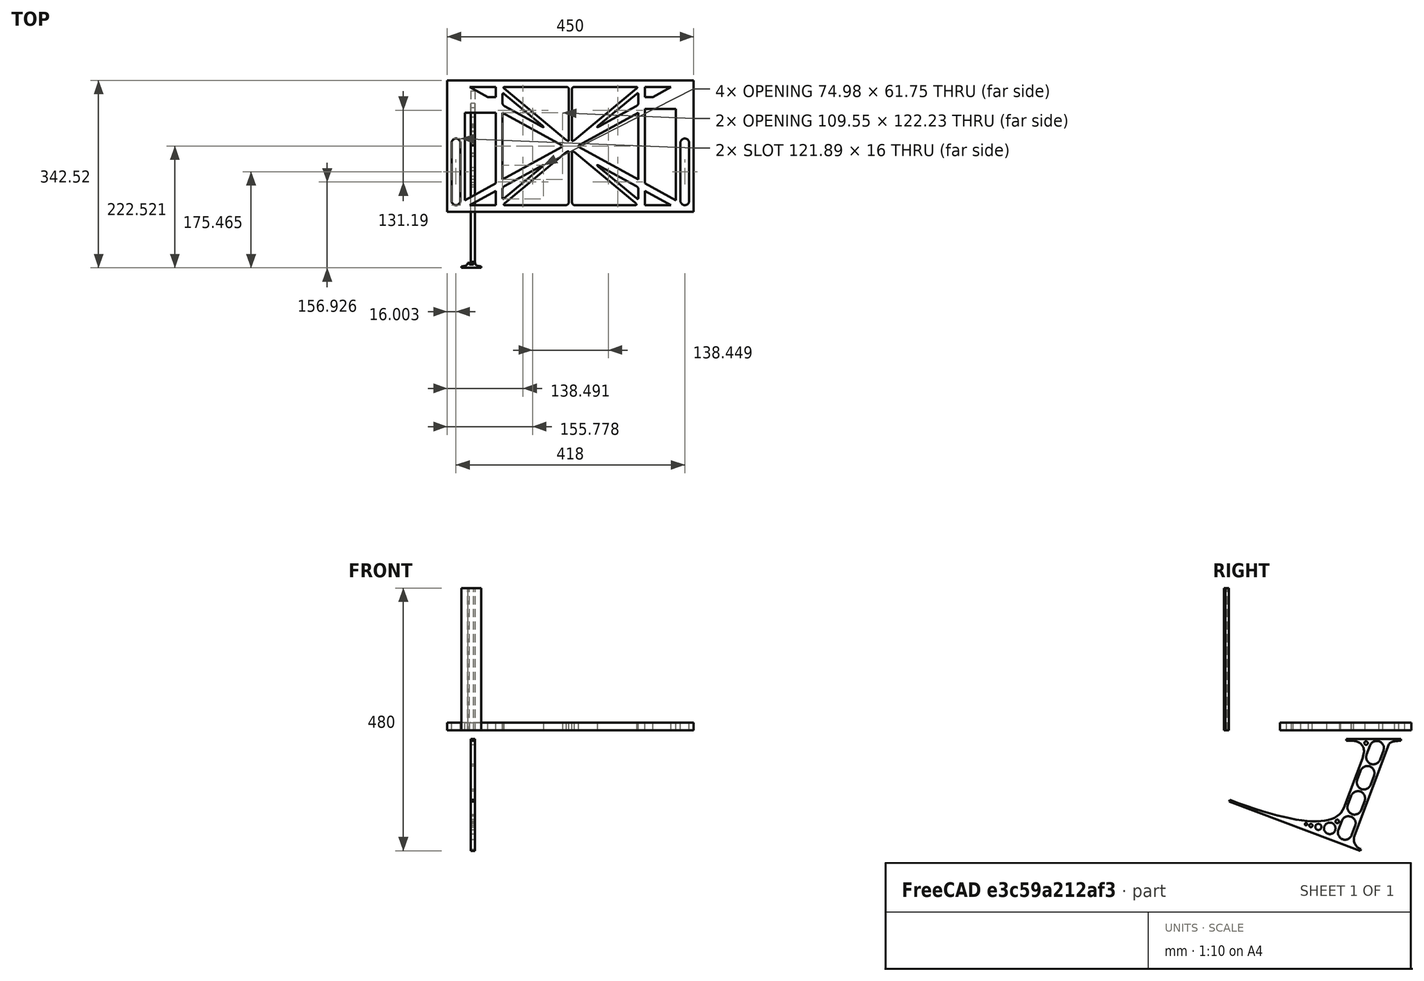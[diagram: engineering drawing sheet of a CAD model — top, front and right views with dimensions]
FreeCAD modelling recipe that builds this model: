
FCSTD DOCUMENT  (FreeCAD 0.19R0.19.2)
Label: laptopStand086
License: All rights reserved
LicenseURL: http://en.wikipedia.org/wiki/All_rights_reserved
objects: Sketcher::SketchObject×3, Part::Extrusion×3
note: 6 computed .brp shape members not serialized (recipe doc carries the construction recipe); baked Part::Feature solids carry a one-line shape summary decoded from their .brp

FEATURE [Sketcher::SketchObject] Sketch
  FullyConstrained = true
  sketch-geometry (224):
    g0: LineSegment StartX=-10.9272 StartY=-82.7794 StartZ=0 EndX=46.0728 EndY=-51.4823 EndZ=0
    g1: LineSegment StartX=366.073 StartY=-91.7794 StartZ=0 EndX=318.073 EndY=-65.424 EndZ=0
    g2: LineSegment StartX=-10.9272 StartY=77.3346 StartZ=0 EndX=-10.9272 EndY=-82.7794 EndZ=0
    g3: LineSegment StartX=375.073 StartY=-82.7794 StartZ=0 EndX=375.073 EndY=83.9235 EndZ=0
    g4: LineSegment StartX=-1.92719 StartY=-91.7794 StartZ=0 EndX=46.0728 EndY=-91.7794 EndZ=0
    g5: LineSegment StartX=318.073 StartY=124.221 StartZ=0 EndX=366.073 EndY=124.221 EndZ=0
    g6: LineSegment StartX=306.073 StartY=77.3346 StartZ=0 EndX=306.073 EndY=-44.8935 EndZ=0
    g7: LineSegment StartX=318.073 StartY=83.9235 StartZ=0 EndX=318.073 EndY=-51.4823 EndZ=0
    g8: LineSegment StartX=318.073 StartY=-51.4823 StartZ=0 EndX=375.073 EndY=-82.7794 EndZ=0
    g9: LineSegment StartX=318.073 StartY=-65.424 StartZ=0 EndX=318.073 EndY=-91.7794 EndZ=0
    g10: LineSegment StartX=318.073 StartY=-91.7794 StartZ=0 EndX=366.073 EndY=-91.7794 EndZ=0
    g11: LineSegment StartX=58.0728 StartY=-44.8935 StartZ=0 EndX=58.0728 EndY=77.3346 EndZ=0
    g12: LineSegment StartX=46.0728 StartY=-65.424 StartZ=0 EndX=-1.92719 EndY=-91.7794 EndZ=0
    g13: LineSegment StartX=46.0728 StartY=-65.424 StartZ=0 EndX=46.0728 EndY=-91.7794 EndZ=0
    g14: LineSegment StartX=46.0728 StartY=77.3346 StartZ=0 EndX=46.0728 EndY=-51.4823 EndZ=0
    g15: LineSegment StartX=-42.9272 StartY=136.221 StartZ=0 EndX=-42.9272 EndY=-103.779 EndZ=0
    g16: LineSegment StartX=407.073 StartY=136.221 StartZ=0 EndX=407.073 EndY=-103.779 EndZ=0
    g17: ArcOfCircle CenterX=-26.9272 CenterY=22.1087 CenterZ=0 NormalX=0 NormalY=0 NormalZ=1 AngleXU=0 Radius=8 StartAngle=1e-16 EndAngle=3.14159
    g18: ArcOfCircle CenterX=-26.9272 CenterY=-83.7794 CenterZ=0 NormalX=0 NormalY=0 NormalZ=1 AngleXU=0 Radius=8 StartAngle=3.14159 EndAngle=6.28319
    g19: LineSegment StartX=-34.9272 StartY=22.1087 StartZ=0 EndX=-34.9272 EndY=-83.7794 EndZ=0
    g20: LineSegment StartX=-18.9272 StartY=22.1087 StartZ=0 EndX=-18.9272 EndY=-83.7794 EndZ=0
    g21: ArcOfCircle CenterX=391.073 CenterY=22.1087 CenterZ=0 NormalX=0 NormalY=0 NormalZ=1 AngleXU=0 Radius=8 StartAngle=-4.4e-15 EndAngle=3.14159
    g22: LineSegment StartX=399.073 StartY=22.1087 StartZ=0 EndX=399.073 EndY=-83.7794 EndZ=0
    g23: LineSegment StartX=383.073 StartY=22.1087 StartZ=0 EndX=383.073 EndY=-83.7794 EndZ=0
    g24: ArcOfCircle CenterX=391.073 CenterY=-83.7794 CenterZ=0 NormalX=0 NormalY=0 NormalZ=1 AngleXU=0 Radius=8 StartAngle=3.14159 EndAngle=6.28319
    g25: Circle CenterX=175.022 CenterY=27.0628 CenterZ=0 NormalX=0 NormalY=0 NormalZ=1 AngleXU=0 Radius=1
    g26: Circle CenterX=179.022 CenterY=24.8665 CenterZ=0 NormalX=0 NormalY=0 NormalZ=1 AngleXU=0 Radius=1
    g27: Circle CenterX=179.022 CenterY=27.0628 CenterZ=0 NormalX=0 NormalY=0 NormalZ=1 AngleXU=0 Radius=1
    g28: BSplineCurve PolesCount=3 KnotsCount=2 Degree=2 IsPeriodic=0
    g29: GeomPoint X=175.022 Y=27.0628 Z=0
    g30: GeomPoint X=179.022 Y=27.0628 Z=0
    g31: Circle CenterX=189.124 CenterY=27.0628 CenterZ=0 NormalX=0 NormalY=0 NormalZ=1 AngleXU=0 Radius=1
    g32: Circle CenterX=185.124 CenterY=24.8665 CenterZ=0 NormalX=0 NormalY=0 NormalZ=1 AngleXU=0 Radius=1
    g33: Circle CenterX=185.124 CenterY=27.0628 CenterZ=0 NormalX=0 NormalY=0 NormalZ=1 AngleXU=0 Radius=1
    g34: BSplineCurve PolesCount=3 KnotsCount=2 Degree=2 IsPeriodic=0
    g35: GeomPoint X=189.124 Y=27.0628 Z=0
    g36: GeomPoint X=185.124 Y=27.0628 Z=0
    g37: Circle CenterX=175.022 CenterY=5.37834 CenterZ=0 NormalX=0 NormalY=0 NormalZ=1 AngleXU=0 Radius=1
    g38: Circle CenterX=179.022 CenterY=7.57463 CenterZ=0 NormalX=0 NormalY=0 NormalZ=1 AngleXU=0 Radius=1
    g39: Circle CenterX=179.022 CenterY=5.34704 CenterZ=0 NormalX=0 NormalY=0 NormalZ=1 AngleXU=0 Radius=1
    g40: BSplineCurve PolesCount=3 KnotsCount=2 Degree=2 IsPeriodic=0
    g41: GeomPoint X=175.022 Y=5.37834 Z=0
    g42: GeomPoint X=179.022 Y=5.34704 Z=0
    g43: Circle CenterX=189.124 CenterY=5.37834 CenterZ=0 NormalX=0 NormalY=0 NormalZ=1 AngleXU=0 Radius=1
    g44: Circle CenterX=185.124 CenterY=7.57463 CenterZ=0 NormalX=0 NormalY=0 NormalZ=1 AngleXU=0 Radius=1
    g45: Circle CenterX=185.124 CenterY=5.34704 CenterZ=0 NormalX=0 NormalY=0 NormalZ=1 AngleXU=0 Radius=1
    g46: BSplineCurve PolesCount=3 KnotsCount=2 Degree=2 IsPeriodic=0
    g47: GeomPoint X=189.124 Y=5.37834 Z=0
    g48: GeomPoint X=185.124 Y=5.34704 Z=0
    g49: Circle CenterX=165.871 CenterY=18.1458 CenterZ=0 NormalX=0 NormalY=0 NormalZ=1 AngleXU=0 Radius=1
    g50: Circle CenterX=169.377 CenterY=16.2206 CenterZ=0 NormalX=0 NormalY=0 NormalZ=1 AngleXU=0 Radius=1
    g51: Circle CenterX=165.871 CenterY=14.2954 CenterZ=0 NormalX=0 NormalY=0 NormalZ=1 AngleXU=0 Radius=1
    g52: BSplineCurve PolesCount=3 KnotsCount=2 Degree=2 IsPeriodic=0
    g53: GeomPoint X=165.871 Y=18.1458 Z=0
    g54: GeomPoint X=165.871 Y=14.2954 Z=0
    g55: Circle CenterX=198.275 CenterY=18.1458 CenterZ=0 NormalX=0 NormalY=0 NormalZ=1 AngleXU=0 Radius=1
    g56: Circle CenterX=194.768 CenterY=16.2206 CenterZ=0 NormalX=0 NormalY=0 NormalZ=1 AngleXU=0 Radius=1
    g57: Circle CenterX=198.275 CenterY=14.2954 CenterZ=0 NormalX=0 NormalY=0 NormalZ=1 AngleXU=0 Radius=1
    g58: BSplineCurve PolesCount=3 KnotsCount=2 Degree=2 IsPeriodic=0
    g59: GeomPoint X=198.275 Y=18.1458 Z=0
    g60: GeomPoint X=198.275 Y=14.2954 Z=0
    g61: LineSegment StartX=165.871 StartY=18.1458 StartZ=0 EndX=58.0728 EndY=77.3346 EndZ=0
    g62: LineSegment StartX=58.0728 StartY=-44.8935 StartZ=0 EndX=165.871 EndY=14.2954 EndZ=0
    g63: LineSegment StartX=198.275 StartY=18.1458 StartZ=0 EndX=306.073 EndY=77.3346 EndZ=0
    g64: LineSegment StartX=198.275 StartY=14.2954 StartZ=0 EndX=306.073 EndY=-44.8935 EndZ=0
    g65: LineSegment StartX=407.073 StartY=-103.779 StartZ=0 EndX=-42.9272 EndY=-103.779 EndZ=0
    g66: LineSegment StartX=407.073 StartY=136.221 StartZ=0 EndX=-42.9272 EndY=136.221 EndZ=0
    g67: LineSegment StartX=46.0728 StartY=77.3346 StartZ=0 EndX=-10.9272 EndY=77.3346 EndZ=0
    g68: LineSegment StartX=46.0728 StartY=105.865 StartZ=0 EndX=31.5028 EndY=105.865 EndZ=0
    g69: LineSegment StartX=46.0728 StartY=124.221 StartZ=0 EndX=46.0728 EndY=105.865 EndZ=0
    g70: LineSegment StartX=-1.92719 StartY=124.221 StartZ=0 EndX=31.5028 EndY=105.865 EndZ=0
    g71: LineSegment StartX=46.0728 StartY=124.221 StartZ=0 EndX=-1.92719 EndY=124.221 EndZ=0
    g72: LineSegment StartX=318.073 StartY=83.9235 StartZ=0 EndX=375.073 EndY=83.9235 EndZ=0
    g73: LineSegment StartX=318.073 StartY=105.865 StartZ=0 EndX=332.643 EndY=105.865 EndZ=0
    g74: LineSegment StartX=332.643 StartY=105.865 StartZ=0 EndX=366.073 EndY=124.221 EndZ=0
    g75: LineSegment StartX=318.073 StartY=124.221 StartZ=0 EndX=318.073 EndY=105.865 EndZ=0
    g76: Circle CenterX=125.607 CenterY=54.1951 CenterZ=0 NormalX=0 NormalY=0 NormalZ=1 AngleXU=0 Radius=1
    g77: Circle CenterX=139.632 CenterY=46.4944 CenterZ=0 NormalX=0 NormalY=0 NormalZ=1 AngleXU=0 Radius=1
    g78: Circle CenterX=127.326 CenterY=56.7187 CenterZ=0 NormalX=0 NormalY=0 NormalZ=1 AngleXU=0 Radius=1
    g79: BSplineCurve PolesCount=3 KnotsCount=2 Degree=2 IsPeriodic=0
    g80: GeomPoint X=125.607 Y=54.1951 Z=0
    g81: GeomPoint X=127.326 Y=56.7187 Z=0
    g82: Circle CenterX=236.821 CenterY=56.7187 CenterZ=0 NormalX=0 NormalY=0 NormalZ=1 AngleXU=0 Radius=1
    g83: Circle CenterX=224.513 CenterY=46.4944 CenterZ=0 NormalX=0 NormalY=0 NormalZ=1 AngleXU=0 Radius=1
    g84: Circle CenterX=238.538 CenterY=54.1951 CenterZ=0 NormalX=0 NormalY=0 NormalZ=1 AngleXU=0 Radius=1
    g85: BSplineCurve PolesCount=3 KnotsCount=2 Degree=2 IsPeriodic=0
    g86: GeomPoint X=236.821 Y=56.7187 Z=0
    g87: GeomPoint X=238.538 Y=54.1951 Z=0
    g88: Circle CenterX=238.538 CenterY=-21.7539 CenterZ=0 NormalX=0 NormalY=0 NormalZ=1 AngleXU=0 Radius=1
    g89: Circle CenterX=224.513 CenterY=-14.0532 CenterZ=0 NormalX=0 NormalY=0 NormalZ=1 AngleXU=0 Radius=1
    g90: Circle CenterX=236.821 CenterY=-24.2775 CenterZ=0 NormalX=0 NormalY=0 NormalZ=1 AngleXU=0 Radius=1
    g91: BSplineCurve PolesCount=3 KnotsCount=2 Degree=2 IsPeriodic=0
    g92: GeomPoint X=238.538 Y=-21.7539 Z=0
    g93: GeomPoint X=236.821 Y=-24.2775 Z=0
    g94: Circle CenterX=125.607 CenterY=-21.7539 CenterZ=0 NormalX=0 NormalY=0 NormalZ=1 AngleXU=0 Radius=1
    g95: Circle CenterX=139.632 CenterY=-14.0532 CenterZ=0 NormalX=0 NormalY=0 NormalZ=1 AngleXU=0 Radius=1
    g96: Circle CenterX=127.325 CenterY=-24.2775 CenterZ=0 NormalX=0 NormalY=0 NormalZ=1 AngleXU=0 Radius=1
    g97: BSplineCurve PolesCount=3 KnotsCount=2 Degree=2 IsPeriodic=0
    g98: GeomPoint X=125.607 Y=-21.7539 Z=0
    g99: GeomPoint X=127.325 Y=-24.2775 Z=0
    g100: Circle CenterX=302.996 CenterY=111.695 CenterZ=0 NormalX=0 NormalY=0 NormalZ=1 AngleXU=0 Radius=1
    g101: Circle CenterX=306.073 CenterY=114.251 CenterZ=0 NormalX=0 NormalY=0 NormalZ=1 AngleXU=0 Radius=1
    g102: Circle CenterX=306.073 CenterY=110.251 CenterZ=0 NormalX=0 NormalY=0 NormalZ=1 AngleXU=0 Radius=1
    g103: BSplineCurve PolesCount=3 KnotsCount=2 Degree=2 IsPeriodic=0
    g104: GeomPoint X=302.996 Y=111.695 Z=0
    g105: GeomPoint X=306.073 Y=110.251 Z=0
    g106: Circle CenterX=306.073 CenterY=95.2763 CenterZ=0 NormalX=0 NormalY=0 NormalZ=1 AngleXU=0 Radius=1
    g107: Circle CenterX=306.073 CenterY=91.2763 CenterZ=0 NormalX=0 NormalY=0 NormalZ=1 AngleXU=0 Radius=1
    g108: Circle CenterX=302.567 CenterY=89.3511 CenterZ=0 NormalX=0 NormalY=0 NormalZ=1 AngleXU=0 Radius=1
    g109: BSplineCurve PolesCount=3 KnotsCount=2 Degree=2 IsPeriodic=0
    g110: GeomPoint X=306.073 Y=95.2763 Z=0
    g111: GeomPoint X=302.567 Y=89.3511 Z=0
    g112: LineSegment StartX=306.073 StartY=110.251 StartZ=0 EndX=306.073 EndY=95.2763 EndZ=0
    g113: LineSegment StartX=302.996 StartY=111.695 StartZ=0 EndX=236.821 EndY=56.7187 EndZ=0
    g114: LineSegment StartX=238.538 StartY=54.1951 StartZ=0 EndX=302.567 EndY=89.3511 EndZ=0
    g115: Circle CenterX=61.1496 CenterY=111.695 CenterZ=0 NormalX=0 NormalY=0 NormalZ=1 AngleXU=0 Radius=1
    g116: Circle CenterX=58.0728 CenterY=114.251 CenterZ=0 NormalX=0 NormalY=0 NormalZ=1 AngleXU=0 Radius=1
    g117: Circle CenterX=58.0728 CenterY=110.251 CenterZ=0 NormalX=0 NormalY=0 NormalZ=1 AngleXU=0 Radius=1
    g118: BSplineCurve PolesCount=3 KnotsCount=2 Degree=2 IsPeriodic=0
    g119: GeomPoint X=61.1496 Y=111.695 Z=0
    g120: GeomPoint X=58.0728 Y=110.251 Z=0
    g121: Circle CenterX=61.5791 CenterY=89.3511 CenterZ=0 NormalX=0 NormalY=0 NormalZ=1 AngleXU=0 Radius=1
    g122: Circle CenterX=58.0728 CenterY=91.2763 CenterZ=0 NormalX=0 NormalY=0 NormalZ=1 AngleXU=0 Radius=1
    g123: Circle CenterX=58.0728 CenterY=95.2763 CenterZ=0 NormalX=0 NormalY=0 NormalZ=1 AngleXU=0 Radius=1
    g124: BSplineCurve PolesCount=3 KnotsCount=2 Degree=2 IsPeriodic=0
    g125: GeomPoint X=61.5791 Y=89.3511 Z=0
    g126: GeomPoint X=58.0728 Y=95.2763 Z=0
    g127: LineSegment StartX=58.0728 StartY=110.251 StartZ=0 EndX=58.0728 EndY=95.2763 EndZ=0
    g128: LineSegment StartX=61.1496 StartY=111.695 StartZ=0 EndX=127.326 EndY=56.7187 EndZ=0
    g129: LineSegment StartX=125.607 StartY=54.1951 StartZ=0 EndX=61.5791 EndY=89.3511 EndZ=0
    g130: Circle CenterX=61.5791 CenterY=-56.9099 CenterZ=0 NormalX=0 NormalY=0 NormalZ=1 AngleXU=0 Radius=1
    g131: Circle CenterX=58.0728 CenterY=-58.8351 CenterZ=0 NormalX=0 NormalY=0 NormalZ=1 AngleXU=0 Radius=1
    g132: Circle CenterX=58.0728 CenterY=-62.8351 CenterZ=0 NormalX=0 NormalY=0 NormalZ=1 AngleXU=0 Radius=1
    g133: BSplineCurve PolesCount=3 KnotsCount=2 Degree=2 IsPeriodic=0
    g134: GeomPoint X=61.5791 Y=-56.9099 Z=0
    g135: GeomPoint X=58.0728 Y=-62.8351 Z=0
    g136: Circle CenterX=58.0728 CenterY=-77.8102 CenterZ=0 NormalX=0 NormalY=0 NormalZ=1 AngleXU=0 Radius=1
    g137: Circle CenterX=58.0728 CenterY=-81.8102 CenterZ=0 NormalX=0 NormalY=0 NormalZ=1 AngleXU=0 Radius=1
    g138: Circle CenterX=61.1496 CenterY=-79.2541 CenterZ=0 NormalX=0 NormalY=0 NormalZ=1 AngleXU=0 Radius=1
    g139: BSplineCurve PolesCount=3 KnotsCount=2 Degree=2 IsPeriodic=0
    g140: GeomPoint X=58.0728 Y=-77.8102 Z=0
    g141: GeomPoint X=61.1496 Y=-79.2541 Z=0
    g142: LineSegment StartX=58.0728 StartY=-62.8351 StartZ=0 EndX=58.0728 EndY=-77.8102 EndZ=0
    g143: LineSegment StartX=61.1496 StartY=-79.2541 StartZ=0 EndX=127.325 EndY=-24.2775 EndZ=0
    g144: LineSegment StartX=125.607 StartY=-21.7539 StartZ=0 EndX=61.5791 EndY=-56.9099 EndZ=0
    g145: Circle CenterX=302.567 CenterY=-56.9099 CenterZ=0 NormalX=0 NormalY=0 NormalZ=1 AngleXU=0 Radius=1
    g146: Circle CenterX=306.073 CenterY=-58.8351 CenterZ=0 NormalX=0 NormalY=0 NormalZ=1 AngleXU=0 Radius=1
    g147: Circle CenterX=306.073 CenterY=-62.8351 CenterZ=0 NormalX=0 NormalY=0 NormalZ=1 AngleXU=0 Radius=1
    g148: BSplineCurve PolesCount=3 KnotsCount=2 Degree=2 IsPeriodic=0
    g149: GeomPoint X=302.567 Y=-56.9099 Z=0
    g150: GeomPoint X=306.073 Y=-62.8351 Z=0
    g151: Circle CenterX=302.996 CenterY=-79.2541 CenterZ=0 NormalX=0 NormalY=0 NormalZ=1 AngleXU=0 Radius=1
    g152: Circle CenterX=306.073 CenterY=-81.8102 CenterZ=0 NormalX=0 NormalY=0 NormalZ=1 AngleXU=0 Radius=1
    g153: Circle CenterX=306.073 CenterY=-77.8102 CenterZ=0 NormalX=0 NormalY=0 NormalZ=1 AngleXU=0 Radius=1
    g154: BSplineCurve PolesCount=3 KnotsCount=2 Degree=2 IsPeriodic=0
    g155: GeomPoint X=302.996 Y=-79.2541 Z=0
    g156: GeomPoint X=306.073 Y=-77.8102 Z=0
    g157: LineSegment StartX=306.073 StartY=-62.8351 StartZ=0 EndX=306.073 EndY=-77.8102 EndZ=0
    g158: LineSegment StartX=302.996 StartY=-79.2541 StartZ=0 EndX=236.821 EndY=-24.2775 EndZ=0
    g159: LineSegment StartX=238.538 StartY=-21.7539 StartZ=0 EndX=302.567 EndY=-56.9099 EndZ=0
    g160: Circle CenterX=61.6457 CenterY=-88.8112 CenterZ=0 NormalX=0 NormalY=0 NormalZ=1 AngleXU=0 Radius=1
    g161: Circle CenterX=58.0728 CenterY=-91.7794 CenterZ=0 NormalX=0 NormalY=0 NormalZ=1 AngleXU=0 Radius=1
    g162: Circle CenterX=63.9135 CenterY=-91.7794 CenterZ=0 NormalX=0 NormalY=0 NormalZ=1 AngleXU=0 Radius=1
    g163: BSplineCurve PolesCount=3 KnotsCount=2 Degree=2 IsPeriodic=0
    g164: GeomPoint X=61.6457 Y=-88.8112 Z=0
    g165: GeomPoint X=63.9135 Y=-91.7794 Z=0
    g166: Circle CenterX=179.022 CenterY=-85.8163 CenterZ=0 NormalX=0 NormalY=0 NormalZ=1 AngleXU=0 Radius=1
    g167: Circle CenterX=179.022 CenterY=-91.7794 CenterZ=0 NormalX=0 NormalY=0 NormalZ=1 AngleXU=0 Radius=1
    g168: Circle CenterX=171.895 CenterY=-91.7794 CenterZ=0 NormalX=0 NormalY=0 NormalZ=1 AngleXU=0 Radius=1
    g169: BSplineCurve PolesCount=3 KnotsCount=2 Degree=2 IsPeriodic=0
    g170: GeomPoint X=179.022 Y=-85.8163 Z=0
    g171: GeomPoint X=171.895 Y=-91.7794 Z=0
    g172: Circle CenterX=185.124 CenterY=-86.2028 CenterZ=0 NormalX=0 NormalY=0 NormalZ=1 AngleXU=0 Radius=1
    g173: Circle CenterX=185.124 CenterY=-91.7794 CenterZ=0 NormalX=0 NormalY=0 NormalZ=1 AngleXU=0 Radius=1
    g174: Circle CenterX=191.747 CenterY=-91.7794 CenterZ=0 NormalX=0 NormalY=0 NormalZ=1 AngleXU=0 Radius=1
    g175: BSplineCurve PolesCount=3 KnotsCount=2 Degree=2 IsPeriodic=0
    g176: GeomPoint X=185.124 Y=-86.2028 Z=0
    g177: GeomPoint X=191.747 Y=-91.7794 Z=0
    g178: Circle CenterX=299.888 CenterY=-86.6413 CenterZ=0 NormalX=0 NormalY=0 NormalZ=1 AngleXU=0 Radius=1
    g179: Circle CenterX=306.073 CenterY=-91.7794 CenterZ=0 NormalX=0 NormalY=0 NormalZ=1 AngleXU=0 Radius=1
    g180: Circle CenterX=298.776 CenterY=-91.7794 CenterZ=0 NormalX=0 NormalY=0 NormalZ=1 AngleXU=0 Radius=1
    g181: BSplineCurve PolesCount=3 KnotsCount=2 Degree=2 IsPeriodic=0
    g182: GeomPoint X=299.888 Y=-86.6413 Z=0
    g183: GeomPoint X=298.776 Y=-91.7794 Z=0
    g184: LineSegment StartX=189.124 StartY=5.37834 StartZ=0 EndX=299.888 EndY=-86.6413 EndZ=0
    g185: LineSegment StartX=298.776 StartY=-91.7794 StartZ=0 EndX=191.747 EndY=-91.7794 EndZ=0
    g186: LineSegment StartX=185.124 StartY=-86.2028 StartZ=0 EndX=185.124 EndY=5.34704 EndZ=0
    g187: LineSegment StartX=179.022 StartY=5.34704 StartZ=0 EndX=179.022 EndY=-85.8163 EndZ=0
    g188: LineSegment StartX=171.895 StartY=-91.7794 StartZ=0 EndX=63.9135 EndY=-91.7794 EndZ=0
    g189: LineSegment StartX=61.6457 StartY=-88.8112 StartZ=0 EndX=175.022 EndY=5.37834 EndZ=0
    g190: Circle CenterX=302.073 CenterY=124.221 CenterZ=0 NormalX=0 NormalY=0 NormalZ=1 AngleXU=0 Radius=1
    g191: Circle CenterX=306.073 CenterY=124.221 CenterZ=0 NormalX=0 NormalY=0 NormalZ=1 AngleXU=0 Radius=1
    g192: Circle CenterX=302.996 CenterY=121.665 CenterZ=0 NormalX=0 NormalY=0 NormalZ=1 AngleXU=0 Radius=1
    g193: BSplineCurve PolesCount=3 KnotsCount=2 Degree=2 IsPeriodic=0
    g194: GeomPoint X=302.073 Y=124.221 Z=0
    g195: GeomPoint X=302.996 Y=121.665 Z=0
    g196: Circle CenterX=189.124 CenterY=124.221 CenterZ=0 NormalX=0 NormalY=0 NormalZ=1 AngleXU=0 Radius=1
    g197: Circle CenterX=185.124 CenterY=124.221 CenterZ=0 NormalX=0 NormalY=0 NormalZ=1 AngleXU=0 Radius=1
    g198: Circle CenterX=185.124 CenterY=120.221 CenterZ=0 NormalX=0 NormalY=0 NormalZ=1 AngleXU=0 Radius=1
    g199: BSplineCurve PolesCount=3 KnotsCount=2 Degree=2 IsPeriodic=0
    g200: GeomPoint X=189.124 Y=124.221 Z=0
    g201: GeomPoint X=185.124 Y=120.221 Z=0
    g202: Circle CenterX=175.022 CenterY=124.221 CenterZ=0 NormalX=0 NormalY=0 NormalZ=1 AngleXU=0 Radius=1
    g203: Circle CenterX=179.022 CenterY=124.221 CenterZ=0 NormalX=0 NormalY=0 NormalZ=1 AngleXU=0 Radius=1
    g204: Circle CenterX=179.022 CenterY=120.221 CenterZ=0 NormalX=0 NormalY=0 NormalZ=1 AngleXU=0 Radius=1
    g205: BSplineCurve PolesCount=3 KnotsCount=2 Degree=2 IsPeriodic=0
    g206: GeomPoint X=175.022 Y=124.221 Z=0
    g207: GeomPoint X=179.022 Y=120.221 Z=0
    g208: Circle CenterX=62.0728 CenterY=124.221 CenterZ=0 NormalX=0 NormalY=0 NormalZ=1 AngleXU=0 Radius=1
    g209: Circle CenterX=58.0728 CenterY=124.221 CenterZ=0 NormalX=0 NormalY=0 NormalZ=1 AngleXU=0 Radius=1
    g210: Circle CenterX=61.1496 CenterY=121.665 CenterZ=0 NormalX=0 NormalY=0 NormalZ=1 AngleXU=0 Radius=1
    g211: BSplineCurve PolesCount=3 KnotsCount=2 Degree=2 IsPeriodic=0
    g212: GeomPoint X=62.0728 Y=124.221 Z=0
    g213: GeomPoint X=61.1496 Y=121.665 Z=0
    g214: LineSegment StartX=62.0728 StartY=124.221 StartZ=0 EndX=175.022 EndY=124.221 EndZ=0
    g215: LineSegment StartX=179.022 StartY=120.221 StartZ=0 EndX=179.022 EndY=27.0628 EndZ=0
    g216: LineSegment StartX=185.124 StartY=27.0628 StartZ=0 EndX=185.124 EndY=120.221 EndZ=0
    g217: LineSegment StartX=189.124 StartY=124.221 StartZ=0 EndX=302.073 EndY=124.221 EndZ=0
    g218: LineSegment StartX=302.996 StartY=121.665 StartZ=0 EndX=189.124 EndY=27.0628 EndZ=0
    g219: LineSegment StartX=175.022 StartY=27.0628 StartZ=0 EndX=61.1496 EndY=121.665 EndZ=0
    g220: LineSegment StartX=58.0728 StartY=77.3346 StartZ=0 EndX=61.5791 EndY=75.4095 EndZ=0
    g221: LineSegment StartX=58.0728 StartY=77.3346 StartZ=0 EndX=58.0728 EndY=73.3346 EndZ=0
    g222: LineSegment StartX=58.0728 StartY=-44.8935 StartZ=0 EndX=58.0728 EndY=-40.8935 EndZ=0
    g223: LineSegment StartX=58.0728 StartY=-44.8935 StartZ=0 EndX=61.5791 EndY=-42.9683 EndZ=0
  constraints (387):
    c: Horizontal(g4)
    c: Horizontal(g5)
    c: Coincident(g7,g8)
    c: Coincident(g9,g1)
    c: Tangent(g7,g9)
    c: Coincident(g13,g12)
    c: Coincident(g0,g14)
    c: Block(g8)
    c: Block(g3)
    c: Block(g1)
    c: Block(g9)
    c: Block(g13)
    c: Block(g12)
    c: Block(g0)
    c: Block(g2)
    c: Block(g6)
    c: Block(g5)
    c: Block(g10)
    c: Block(g4)
    c: Vertical(g15)
    c: Vertical(g16)
    c: Block(g16)
    c: Block(g15)
    c: Tangent(g17,g20) = 1.5708
    c: Tangent(g17,g19) = -1.5708
    c: Tangent(g19,g18) = -1.5708
    c: Tangent(g20,g18) = 1.5708
    c: Vertical(g19)
    c: Equal(g17,g18)
    c: Block(g20)
    c: Block(g19)
    c: Tangent(g21,g22) = 1.5708
    c: Tangent(g22,g24) = 1.5708
    c: Equal(g21,g24)
    c: Coincident(g23,g21)
    c: Coincident(g23,g24)
    c: Block(g22)
    c: Block(g23)
    c: Weight(g25) = 1
    c: Equal(g25,g26)
    c: Equal(g25,g27)
    c: InternalAlignment(g25,g28)
    c: InternalAlignment(g26,g28)
    c: InternalAlignment(g27,g28)
    c: InternalAlignment(g29,g28)
    c: InternalAlignment(g30,g28)
    c: Weight(g31) = 1
    c: Equal(g31,g32)
    c: Equal(g31,g33)
    c: InternalAlignment(g31,g34)
    c: InternalAlignment(g32,g34)
    c: InternalAlignment(g33,g34)
    c: InternalAlignment(g35,g34)
    c: InternalAlignment(g36,g34)
    c: Block(g34)
    c: Block(g28)
    c: Weight(g37) = 1
    c: Equal(g37,g38)
    c: Equal(g37,g39)
    c: InternalAlignment(g37,g40)
    c: InternalAlignment(g38,g40)
    c: InternalAlignment(g39,g40)
    c: InternalAlignment(g41,g40)
    c: InternalAlignment(g42,g40)
    c: Weight(g43) = 1
    c: Equal(g43,g44)
    c: Equal(g43,g45)
    c: InternalAlignment(g43,g46)
    c: InternalAlignment(g44,g46)
    c: InternalAlignment(g45,g46)
    c: InternalAlignment(g47,g46)
    c: InternalAlignment(g48,g46)
    c: Block(g46)
    c: Block(g40)
    c: Weight(g49) = 1
    c: Equal(g49,g50)
    c: Equal(g49,g51)
    c: InternalAlignment(g49,g52)
    c: InternalAlignment(g50,g52)
    c: InternalAlignment(g51,g52)
    c: InternalAlignment(g53,g52)
    c: InternalAlignment(g54,g52)
    c: Weight(g55) = 1
    c: Equal(g55,g56)
    c: Equal(g55,g57)
    c: InternalAlignment(g55,g58)
    c: InternalAlignment(g56,g58)
    c: InternalAlignment(g57,g58)
    c: InternalAlignment(g59,g58)
    c: InternalAlignment(g60,g58)
    c: Block(g52)
    c: Block(g58)
    c: Coincident(g61,g52)
    c: Coincident(g61,g11)
    c: Coincident(g62,g11)
    c: Coincident(g62,g52)
    c: Coincident(g63,g58)
    c: Coincident(g63,g6)
    c: Coincident(g64,g58)
    c: Coincident(g64,g6)
    c: Block(g11)
    c: Coincident(g65,g16)
    c: Coincident(g65,g15)
    c: Horizontal(g65)
    c: Distance(g65) = 450
    c: Coincident(g66,g16)
    c: Coincident(g66,g15)
    c: Horizontal(g66)
    c: Horizontal(g67)
    c: Coincident(g14,g67)
    c: Horizontal(g68)
    c: Vertical(g69)
    c: Block(g69)
    c: Block(g68)
    c: Block(g67)
    c: Distance(g69) = 18.3554
    c: Coincident(g71,g69)
    c: Coincident(g71,g70)
    c: Horizontal(g71)
    c: Block(g71)
    c: Block(g70)
    c: Coincident(g68,g70)
    c: Coincident(g2,g67)
    c: Coincident(g72,g7)
    c: Horizontal(g72)
    c: Horizontal(g73)
    c: Block(g72)
    c: Coincident(g74,g5)
    c: Coincident(g75,g5)
    c: Coincident(g75,g73)
    c: Vertical(g75)
    c: Block(g75)
    c: Coincident(g73,g74)
    c: Block(g74)
    c: Coincident(g3,g72)
    c: Weight(g76) = 1
    c: Equal(g76,g77)
    c: Equal(g76,g78)
    c: InternalAlignment(g76,g79)
    c: InternalAlignment(g77,g79)
    c: InternalAlignment(g78,g79)
    c: InternalAlignment(g80,g79)
    c: InternalAlignment(g81,g79)
    c: Block(g79)
    c: Weight(g82) = 1
    c: Equal(g82,g83)
    c: Equal(g82,g84)
    c: InternalAlignment(g82,g85)
    c: InternalAlignment(g83,g85)
    c: InternalAlignment(g84,g85)
    c: InternalAlignment(g86,g85)
    c: InternalAlignment(g87,g85)
    c: Block(g85)
    c: Weight(g88) = 1
    c: Equal(g88,g89)
    c: Equal(g88,g90)
    c: InternalAlignment(g88,g91)
    c: InternalAlignment(g89,g91)
    c: InternalAlignment(g90,g91)
    c: InternalAlignment(g92,g91)
    c: InternalAlignment(g93,g91)
    c: Block(g91)
    c: Weight(g94) = 1
    c: Equal(g94,g95)
    c: Equal(g94,g96)
    c: InternalAlignment(g94,g97)
    c: InternalAlignment(g95,g97)
    c: InternalAlignment(g96,g97)
    c: InternalAlignment(g98,g97)
    c: InternalAlignment(g99,g97)
    c: Block(g97)
    c: Weight(g100) = 1
    c: Equal(g100,g101)
    c: Equal(g100,g102)
    c: InternalAlignment(g100,g103)
    c: InternalAlignment(g101,g103)
    c: InternalAlignment(g102,g103)
    c: InternalAlignment(g104,g103)
    c: InternalAlignment(g105,g103)
    c: Weight(g106) = 1
    c: Equal(g106,g107)
    c: Equal(g106,g108)
    c: InternalAlignment(g106,g109)
    c: InternalAlignment(g107,g109)
    c: InternalAlignment(g108,g109)
    c: InternalAlignment(g110,g109)
    c: InternalAlignment(g111,g109)
    c: Block(g103)
    c: Block(g109)
    c: Coincident(g112,g103)
    c: Coincident(g112,g109)
    c: Vertical(g112)
    c: Coincident(g113,g103)
    c: Coincident(g113,g85)
    c: Coincident(g114,g85)
    c: Coincident(g114,g109)
    c: Weight(g115) = 1
    c: Equal(g115,g116)
    c: Equal(g115,g117)
    c: InternalAlignment(g115,g118)
    c: InternalAlignment(g116,g118)
    c: InternalAlignment(g117,g118)
    c: InternalAlignment(g119,g118)
    c: InternalAlignment(g120,g118)
    c: Weight(g121) = 1
    c: Equal(g121,g122)
    c: Equal(g121,g123)
    c: InternalAlignment(g121,g124)
    c: InternalAlignment(g122,g124)
    c: InternalAlignment(g123,g124)
    c: InternalAlignment(g125,g124)
    c: InternalAlignment(g126,g124)
    c: Block(g118)
    c: Block(g124)
    c: Coincident(g127,g118)
    c: Coincident(g127,g124)
    c: Vertical(g127)
    c: Coincident(g128,g118)
    c: Coincident(g128,g79)
    c: Coincident(g129,g79)
    c: Coincident(g129,g124)
    c: Weight(g130) = 1
    c: Equal(g130,g131)
    c: Equal(g130,g132)
    c: InternalAlignment(g130,g133)
    c: InternalAlignment(g131,g133)
    c: InternalAlignment(g132,g133)
    c: InternalAlignment(g134,g133)
    c: InternalAlignment(g135,g133)
    c: Weight(g136) = 1
    c: Equal(g136,g137)
    c: Equal(g136,g138)
    c: InternalAlignment(g136,g139)
    c: InternalAlignment(g137,g139)
    c: InternalAlignment(g138,g139)
    c: InternalAlignment(g140,g139)
    c: InternalAlignment(g141,g139)
    c: Block(g133)
    c: Block(g139)
    c: Coincident(g142,g133)
    c: Coincident(g142,g139)
    c: Vertical(g142)
    c: Coincident(g143,g139)
    c: Coincident(g143,g97)
    c: Coincident(g144,g97)
    c: Coincident(g144,g133)
    c: Weight(g145) = 1
    c: Equal(g145,g146)
    c: Equal(g145,g147)
    c: InternalAlignment(g145,g148)
    c: InternalAlignment(g146,g148)
    c: InternalAlignment(g147,g148)
    c: InternalAlignment(g149,g148)
    c: InternalAlignment(g150,g148)
    c: Weight(g151) = 1
    c: Equal(g151,g152)
    c: Equal(g151,g153)
    c: InternalAlignment(g151,g154)
    c: InternalAlignment(g152,g154)
    c: InternalAlignment(g153,g154)
    c: InternalAlignment(g155,g154)
    c: InternalAlignment(g156,g154)
    c: Block(g148)
    c: Block(g154)
    c: Coincident(g157,g148)
    c: Coincident(g157,g154)
    c: Vertical(g157)
    c: Coincident(g158,g154)
    c: Coincident(g158,g91)
    c: Coincident(g159,g91)
    c: Coincident(g159,g148)
    c: Weight(g160) = 1
    c: Equal(g160,g161)
    c: Equal(g160,g162)
    c: InternalAlignment(g160,g163)
    c: InternalAlignment(g161,g163)
    c: InternalAlignment(g162,g163)
    c: InternalAlignment(g164,g163)
    c: InternalAlignment(g165,g163)
    c: Weight(g166) = 1
    c: Equal(g166,g167)
    c: Equal(g166,g168)
    c: InternalAlignment(g166,g169)
    c: InternalAlignment(g167,g169)
    c: InternalAlignment(g168,g169)
    c: InternalAlignment(g170,g169)
    c: InternalAlignment(g171,g169)
    c: Weight(g172) = 1
    c: Equal(g172,g173)
    c: Equal(g172,g174)
    c: InternalAlignment(g172,g175)
    c: InternalAlignment(g173,g175)
    c: InternalAlignment(g174,g175)
    c: InternalAlignment(g176,g175)
    c: InternalAlignment(g177,g175)
    c: Weight(g178) = 1
    c: Equal(g178,g179)
    c: Equal(g178,g180)
    c: InternalAlignment(g178,g181)
    c: InternalAlignment(g179,g181)
    c: InternalAlignment(g180,g181)
    c: InternalAlignment(g182,g181)
    c: InternalAlignment(g183,g181)
    c: Block(g181)
    c: Block(g175)
    c: Block(g169)
    c: Block(g163)
    c: Coincident(g184,g46)
    c: Coincident(g184,g181)
    c: Coincident(g185,g181)
    c: Coincident(g185,g175)
    c: Horizontal(g185)
    c: Coincident(g186,g175)
    c: Coincident(g186,g46)
    c: Vertical(g186)
    c: Coincident(g187,g40)
    c: Coincident(g187,g169)
    c: Vertical(g187)
    c: Coincident(g188,g169)
    c: Coincident(g188,g163)
    c: Horizontal(g188)
    c: Coincident(g189,g163)
    c: Coincident(g189,g40)
    c: Weight(g190) = 1
    c: Equal(g190,g191)
    c: Equal(g190,g192)
    c: InternalAlignment(g190,g193)
    c: InternalAlignment(g191,g193)
    c: InternalAlignment(g192,g193)
    c: InternalAlignment(g194,g193)
    c: InternalAlignment(g195,g193)
    c: Weight(g196) = 1
    c: Equal(g196,g197)
    c: Equal(g196,g198)
    c: InternalAlignment(g196,g199)
    c: InternalAlignment(g197,g199)
    c: InternalAlignment(g198,g199)
    c: InternalAlignment(g200,g199)
    c: InternalAlignment(g201,g199)
    c: Weight(g202) = 1
    c: Equal(g202,g203)
    c: Equal(g202,g204)
    c: InternalAlignment(g202,g205)
    c: InternalAlignment(g203,g205)
    c: InternalAlignment(g204,g205)
    c: InternalAlignment(g206,g205)
    c: InternalAlignment(g207,g205)
    c: Weight(g208) = 1
    c: Equal(g208,g209)
    c: Equal(g208,g210)
    c: InternalAlignment(g208,g211)
    c: InternalAlignment(g209,g211)
    c: InternalAlignment(g210,g211)
    c: InternalAlignment(g212,g211)
    c: InternalAlignment(g213,g211)
    c: Block(g211)
    c: Block(g205)
    c: Block(g199)
    c: Block(g193)
    c: Coincident(g214,g211)
    c: Coincident(g214,g205)
    c: Horizontal(g214)
    c: Coincident(g215,g205)
    c: Coincident(g215,g28)
    c: Vertical(g215)
    c: Coincident(g216,g34)
    c: Coincident(g216,g199)
    c: Vertical(g216)
    c: Coincident(g217,g199)
    c: Coincident(g217,g193)
    c: Horizontal(g217)
    c: Coincident(g218,g193)
    c: Coincident(g218,g34)
    c: Coincident(g219,g28)
    c: Coincident(g219,g211)
    c: Vertical(g221)
    c: Vertical(g222)
    c: Parallel(g62,g223)
    c: Parallel(g220,g61)
    c: Distance(g220) = 4
    c: Distance(g221) = 4
    c: Distance(g222) = 4
    c: Distance(g223) = 4
    c: Coincident(g223,g11)
    c: Coincident(g222,g11)
    c: Coincident(g220,g11)
    c: Coincident(g11,g221)
FEATURE [Sketcher::SketchObject] Sketch001
  FullyConstrained = true
  MapMode = 4
  Placement = pos=(0,0,0) rot=(0.57735,0.57735,0.57735;2.0944rad)
  Support = -> [Sketch]
  sketch-geometry (46):
    g0: BSplineCurve PolesCount=3 KnotsCount=2 Degree=2 IsPeriodic=0
    g1: ArcOfCircle CenterX=73.1223 CenterY=-32.291 CenterZ=0 NormalX=0 NormalY=0 NormalZ=1 AngleXU=0 Radius=13 StartAngle=5.92268 EndAngle=9.06428
    g2: ArcOfCircle CenterX=66.7816 CenterY=-49.1439 CenterZ=0 NormalX=0 NormalY=0 NormalZ=1 AngleXU=0 Radius=13 StartAngle=2.78068 EndAngle=5.92131
    g3: ArcOfCircle CenterX=55.9263 CenterY=-78.1807 CenterZ=0 NormalX=0 NormalY=0 NormalZ=1 AngleXU=0 Radius=13 StartAngle=5.92268 EndAngle=9.06428
    g4: ArcOfCircle CenterX=49.5884 CenterY=-95.0342 CenterZ=0 NormalX=0 NormalY=0 NormalZ=1 AngleXU=0 Radius=13 StartAngle=2.78068 EndAngle=5.92131
    g5: ArcOfCircle CenterX=38.7206 CenterY=-124.067 CenterZ=0 NormalX=0 NormalY=0 NormalZ=1 AngleXU=0 Radius=13 StartAngle=5.92268 EndAngle=9.06428
    g6: ArcOfCircle CenterX=32.3875 CenterY=-140.92 CenterZ=0 NormalX=0 NormalY=0 NormalZ=1 AngleXU=0 Radius=13 StartAngle=2.78068 EndAngle=5.92131
    g7: ArcOfCircle CenterX=21.4715 CenterY=-169.934 CenterZ=0 NormalX=0 NormalY=0 NormalZ=1 AngleXU=0 Radius=13 StartAngle=5.92268 EndAngle=9.06428
    g8: ArcOfCircle CenterX=15.1336 CenterY=-186.787 CenterZ=0 NormalX=0 NormalY=0 NormalZ=1 AngleXU=0 Radius=13 StartAngle=2.78068 EndAngle=5.92131
    g9-g12: Circle x4 (B-spline internal-alignment scaffolding for g13; pole/knot coordinates omitted)
    g13: BSplineCurve PolesCount=4 KnotsCount=2 Degree=3 IsPeriodic=0
    g14: GeomPoint X=28.8094 Y=-19.0875 Z=0
    g15: GeomPoint X=47.0443 Y=-50.4712 Z=0
    g16: Circle CenterX=53.5586 CenterY=-23.2695 CenterZ=0 NormalX=0 NormalY=0 NormalZ=1 AngleXU=0 Radius=3.24518
    g17: Circle CenterX=-195.441 CenterY=-127.082 CenterZ=0 NormalX=0 NormalY=0 NormalZ=1 AngleXU=0 Radius=1
    g18: Circle CenterX=-8.24091 CenterY=-197.481 CenterZ=0 NormalX=0 NormalY=0 NormalZ=1 AngleXU=0 Radius=1
    g19: Circle CenterX=12.8789 CenterY=-141.321 CenterZ=0 NormalX=0 NormalY=0 NormalZ=1 AngleXU=0 Radius=1
    g20: BSplineCurve PolesCount=3 KnotsCount=2 Degree=2 IsPeriodic=0
    g21: GeomPoint X=-195.441 Y=-127.082 Z=0
    g22: GeomPoint X=12.8789 Y=-141.321 Z=0
    g23: Circle CenterX=-12.8016 CenterY=-179.036 CenterZ=0 NormalX=0 NormalY=0 NormalZ=1 AngleXU=0 Radius=10.5072
    g24: Circle CenterX=0.933922 CenterY=-166.43 CenterZ=0 NormalX=0 NormalY=0 NormalZ=1 AngleXU=0 Radius=3.26661
    g25: Circle CenterX=-33.5518 CenterY=-176.44 CenterZ=0 NormalX=0 NormalY=0 NormalZ=1 AngleXU=0 Radius=5.64388
    g26: Circle CenterX=-47.2366 CenterY=-173.859 CenterZ=0 NormalX=0 NormalY=0 NormalZ=1 AngleXU=0 Radius=3.01653
    g27: Circle CenterX=-56.2595 CenterY=-171.456 CenterZ=0 NormalX=0 NormalY=0 NormalZ=1 AngleXU=0 Radius=2.12826
    g28: ArcOfCircle CenterX=51.2151 CenterY=-198.473 CenterZ=0 NormalX=0 NormalY=0 NormalZ=1 AngleXU=0 Radius=20 StartAngle=2.78189 EndAngle=4.35269
    g29: LineSegment StartX=32.4951 StartY=-191.433 StartZ=0 EndX=94.6578 EndY=-26.1352 EndZ=0
    g30: LineSegment StartX=43.1192 StartY=-220.001 StartZ=0 EndX=-196.497 EndY=-129.89 EndZ=0
    g31: LineSegment StartX=43.1192 StartY=-220.001 StartZ=0 EndX=44.1752 EndY=-217.193 EndZ=0
    g32: LineSegment StartX=117.223 StartY=-19.0875 StartZ=0 EndX=117.223 EndY=-16.0875 EndZ=0
    g33: LineSegment StartX=117.223 StartY=-16.0875 StartZ=0 EndX=17.2232 EndY=-16.0875 EndZ=0
    g34: LineSegment StartX=17.2232 StartY=-16.0875 StartZ=0 EndX=17.2232 EndY=-19.0875 EndZ=0
    g35: LineSegment StartX=28.8094 StartY=-19.0875 StartZ=0 EndX=17.2232 EndY=-19.0875 EndZ=0
    g36: LineSegment StartX=47.0443 StartY=-50.4712 StartZ=0 EndX=12.8789 EndY=-141.321 EndZ=0
    g37: LineSegment StartX=-195.441 StartY=-127.082 StartZ=0 EndX=-196.497 EndY=-129.89 EndZ=0
    g38: LineSegment StartX=85.2866 StartY=-36.8766 StartZ=0 EndX=78.9396 EndY=-53.7463 EndZ=0
    g39: LineSegment StartX=60.9579 StartY=-27.7053 StartZ=0 EndX=54.6191 EndY=-44.5532 EndZ=0
    g40: LineSegment StartX=68.0907 StartY=-82.7664 StartZ=0 EndX=61.7465 EndY=-99.6365 EndZ=0
    g41: LineSegment StartX=43.7619 StartY=-73.595 StartZ=0 EndX=37.426 EndY=-90.4435 EndZ=0
    g42: LineSegment StartX=50.885 StartY=-128.652 StartZ=0 EndX=44.5456 EndY=-145.522 EndZ=0
    g43: LineSegment StartX=26.5562 StartY=-119.481 StartZ=0 EndX=20.2251 EndY=-136.329 EndZ=0
    g44: LineSegment StartX=9.3071 StartY=-165.349 StartZ=0 EndX=2.97115 EndY=-182.197 EndZ=0
    g45: LineSegment StartX=33.6358 StartY=-174.52 StartZ=0 EndX=27.2917 EndY=-191.39 EndZ=0
  constraints (71):
    c: Block(g0)
    c: Block(g1)
    c: Block(g2)
    c: Block(g4)
    c: Block(g3)
    c: Block(g6)
    c: Block(g5)
    c: Block(g8)
    c: Block(g7)
    c: Weight(g9) = 1
    c: Equal(g9,g10)
    c: Equal(g9,g11)
    c: Equal(g9,g12)
    c: InternalAlignment(g9-g12 -> g13) x4
    c: InternalAlignment(g14,g13)
    c: InternalAlignment(g15,g13)
    c: Block(g16)
    c: Weight(g17) = 1
    c: Equal(g17,g18)
    c: Equal(g17,g19)
    c: InternalAlignment(g17,g20)
    c: InternalAlignment(g18,g20)
    c: InternalAlignment(g19,g20)
    c: InternalAlignment(g21,g20)
    c: InternalAlignment(g22,g20)
    c: Block(g20)
    c: Block(g23)
    c: Block(g24)
    c: Block(g25)
    c: Block(g26)
    c: Block(g27)
    c: Block(g28)
    c: Coincident(g29,g28)
    c: Coincident(g29,g0)
    c: Block(g13)
    c: Coincident(g31,g30)
    c: Coincident(g31,g28)
    c: Block(g31)
    c: Coincident(g32,g0)
    c: Vertical(g32)
    c: Coincident(g33,g32)
    c: Horizontal(g33)
    c: Coincident(g34,g33)
    c: Vertical(g34)
    c: Block(g33)
    c: Coincident(g35,g13)
    c: Coincident(g35,g34)
    c: Horizontal(g35)
    c: Coincident(g36,g13)
    c: Coincident(g36,g20)
    c: Coincident(g37,g20)
    c: Coincident(g37,g30)
    c: Block(g30)
    c: Coincident(g38,g1)
    c: Coincident(g38,g2)
    c: Coincident(g39,g1)
    c: Coincident(g39,g2)
    c: Coincident(g40,g3)
    c: Coincident(g40,g4)
    c: Coincident(g41,g3)
    c: Coincident(g41,g4)
    c: Coincident(g42,g5)
    c: Coincident(g42,g6)
    c: Coincident(g43,g5)
    c: Coincident(g43,g6)
    c: Coincident(g44,g7)
    c: Coincident(g44,g8)
    c: Coincident(g45,g7)
    c: Coincident(g45,g8)
    c: Distance(g30) = 256
    c: Distance(g33) = 100
FEATURE [Part::Extrusion] Extrude002
  Base = -> Sketch001
  Dir = (1,0,0)
  DirMode = 2
  FaceMakerClass = Part::FaceMakerBullseye
  LengthFwd = 8
  LengthRev = 0
  Solid = true
  Symmetric = false
FEATURE [Sketcher::SketchObject] Sketch002
  FullyConstrained = true
  sketch-geometry (20):
    g0: LineSegment StartX=-2.77179 StartY=-200.304 StartZ=0 EndX=5.22821 EndY=-200.304 EndZ=0
    g1: LineSegment StartX=5.22821 StartY=-200.304 StartZ=0 EndX=5.22821 EndY=-197.304 EndZ=0
    g2: LineSegment StartX=-2.77179 StartY=-200.304 StartZ=0 EndX=-2.77179 EndY=-197.304 EndZ=0
    g3: LineSegment StartX=5.22821 StartY=-197.304 StartZ=0 EndX=8.22821 EndY=-197.304 EndZ=0
    g4: LineSegment StartX=-2.77179 StartY=-197.304 StartZ=0 EndX=-5.77179 EndY=-197.304 EndZ=0
    g5: LineSegment StartX=19.2282 StartY=-203.304 StartZ=0 EndX=19.2282 EndY=-206.304 EndZ=0
    g6: LineSegment StartX=-16.7718 StartY=-203.304 StartZ=0 EndX=-16.7718 EndY=-206.304 EndZ=0
    g7: LineSegment StartX=-16.7718 StartY=-206.304 StartZ=0 EndX=19.2282 EndY=-206.304 EndZ=0
    g8: Circle CenterX=-16.7718 CenterY=-203.304 CenterZ=0 NormalX=0 NormalY=0 NormalZ=1 AngleXU=0 Radius=1
    g9: Circle CenterX=-5.77179 CenterY=-203.304 CenterZ=0 NormalX=0 NormalY=0 NormalZ=1 AngleXU=0 Radius=1
    g10: Circle CenterX=-5.77179 CenterY=-197.304 CenterZ=0 NormalX=0 NormalY=0 NormalZ=1 AngleXU=0 Radius=1
    g11: BSplineCurve PolesCount=3 KnotsCount=2 Degree=2 IsPeriodic=0
    g12: GeomPoint X=-16.7718 Y=-203.304 Z=0
    g13: GeomPoint X=-5.77179 Y=-197.304 Z=0
    g14: Circle CenterX=19.2282 CenterY=-203.304 CenterZ=0 NormalX=0 NormalY=0 NormalZ=1 AngleXU=0 Radius=1
    g15: Circle CenterX=8.22821 CenterY=-203.304 CenterZ=0 NormalX=0 NormalY=0 NormalZ=1 AngleXU=0 Radius=1
    g16: Circle CenterX=8.22821 CenterY=-197.304 CenterZ=0 NormalX=0 NormalY=0 NormalZ=1 AngleXU=0 Radius=1
    g17: BSplineCurve PolesCount=3 KnotsCount=2 Degree=2 IsPeriodic=0
    g18: GeomPoint X=19.2282 Y=-203.304 Z=0
    g19: GeomPoint X=8.22821 Y=-197.304 Z=0
  constraints (41):
    c: Horizontal(g0)
    c: Distance(g0) = 8
    c: Coincident(g1,g0)
    c: Vertical(g1)
    c: Distance(g1) = 3
    c: Coincident(g2,g0)
    c: Vertical(g2)
    c: Distance(g2) = 3
    c: Coincident(g3,g1)
    c: Horizontal(g3)
    c: Distance(g3) = 3
    c: Coincident(g4,g2)
    c: Horizontal(g4)
    c: Distance(g4) = 3
    c: Vertical(g5)
    c: Vertical(g6)
    c: Coincident(g7,g6)
    c: Coincident(g7,g5)
    c: Weight(g8) = 1
    c: Equal(g8,g9)
    c: Equal(g8,g10)
    c: Coincident(g11,g4)
    c: InternalAlignment(g8,g11)
    c: InternalAlignment(g9,g11)
    c: InternalAlignment(g10,g11)
    c: InternalAlignment(g12,g11)
    c: InternalAlignment(g13,g11)
    c: Coincident(g17,g5)
    c: Weight(g14) = 1
    c: Equal(g14,g15)
    c: Equal(g14,g16)
    c: Coincident(g17,g3)
    c: InternalAlignment(g14,g17)
    c: InternalAlignment(g15,g17)
    c: InternalAlignment(g16,g17)
    c: InternalAlignment(g18,g17)
    c: InternalAlignment(g19,g17)
    c: Block(g7)
    c: Block(g17)
    c: Block(g11)
    c: Block(g6)
FEATURE [Part::Extrusion] Extrude003
  Base = -> Sketch002
  Dir = (0,0,1)
  DirMode = 2
  FaceMakerClass = Part::FaceMakerBullseye
  LengthFwd = 260
  LengthRev = 0
  Solid = true
  Symmetric = false
FEATURE [Part::Extrusion] Extrude
  Base = -> Sketch
  Dir = (0,0,1)
  DirMode = 2
  FaceMakerClass = Part::FaceMakerBullseye
  LengthFwd = 14
  LengthRev = 0
  Solid = true
  Symmetric = false
